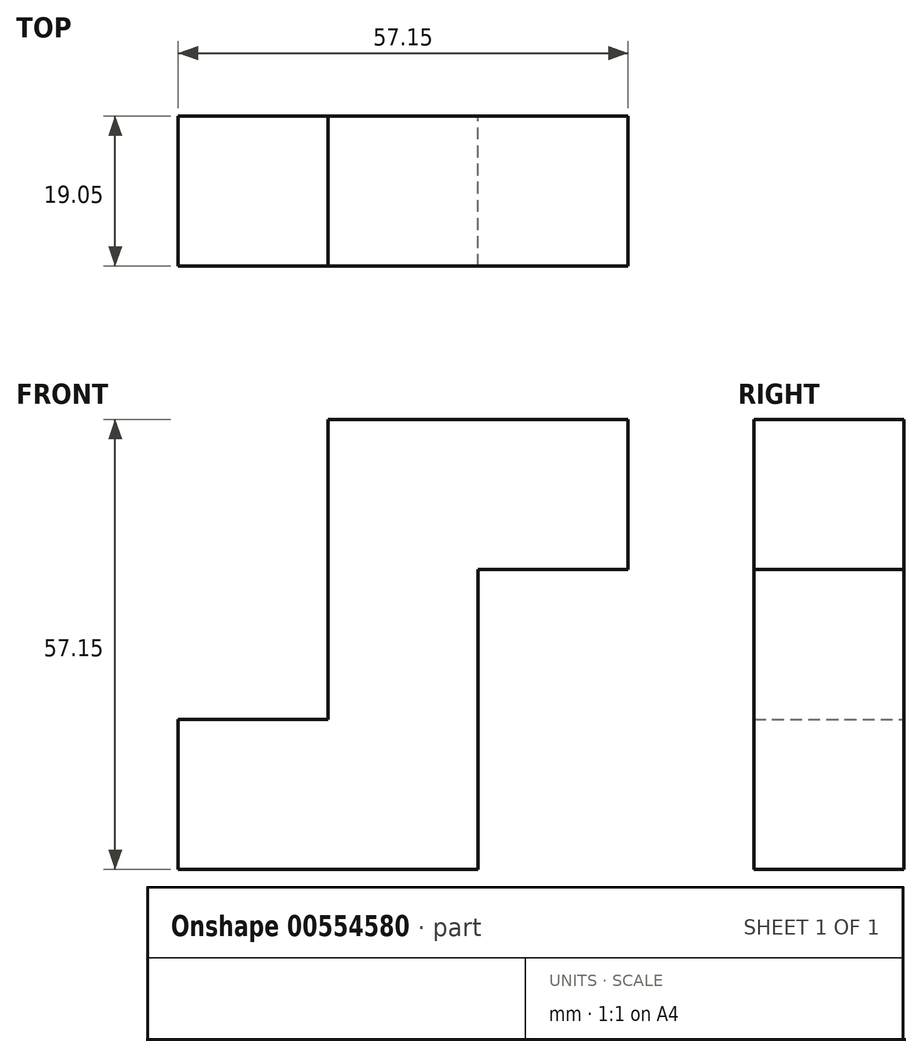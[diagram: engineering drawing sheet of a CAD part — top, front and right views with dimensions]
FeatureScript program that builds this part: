
annotation { "Feature Type Name" : "Feature", "Feature Type Description" : "" }
export const myFeature = defineFeature(function(context is Context, id is Id, definition is map)
    precondition{}
    {
        {
            var Q0;
            Q0=qCreatedBy(makeId("Front.planeOp"),FACE);
            var sketch = newSketch(context, id + "F0", { "sketchPlane" : qUnion([Q0])});
            skLineSegment(sketch, "E0", {"start": v(17.11, 16.65) * mm, "end": v(-20.99, 16.65) * mm});
            skLineSegment(sketch, "E1", {"start": v(-20.99, 16.65) * mm, "end": v(-20.99, -21.45) * mm});
            skLineSegment(sketch, "E2", {"start": v(-20.99, -21.45) * mm, "end": v(-40.04, -21.45) * mm});
            skLineSegment(sketch, "E3", {"start": v(-40.04, -21.45) * mm, "end": v(-40.04, -40.5) * mm});
            skLineSegment(sketch, "E4", {"start": v(-40.04, -40.5) * mm, "end": v(-1.94, -40.5) * mm});
            skLineSegment(sketch, "E5", {"start": v(-1.94, -40.5) * mm, "end": v(-1.94, -2.4) * mm});
            skLineSegment(sketch, "E6", {"start": v(-1.94, -2.4) * mm, "end": v(17.11, -2.4) * mm});
            skLineSegment(sketch, "E7", {"start": v(17.11, -2.4) * mm, "end": v(17.11, 16.65) * mm});
            skSolve(sketch);
        }
        {
            var Q0;
            Q0 = qSketchRegion(id + "F0", true);
            extrude(context, id + "F1", {"entities" : qUnion([Q0]), "depth" : 19.05 * mm, "offsetDistance" : 25.4 * mm});
        }
    });
